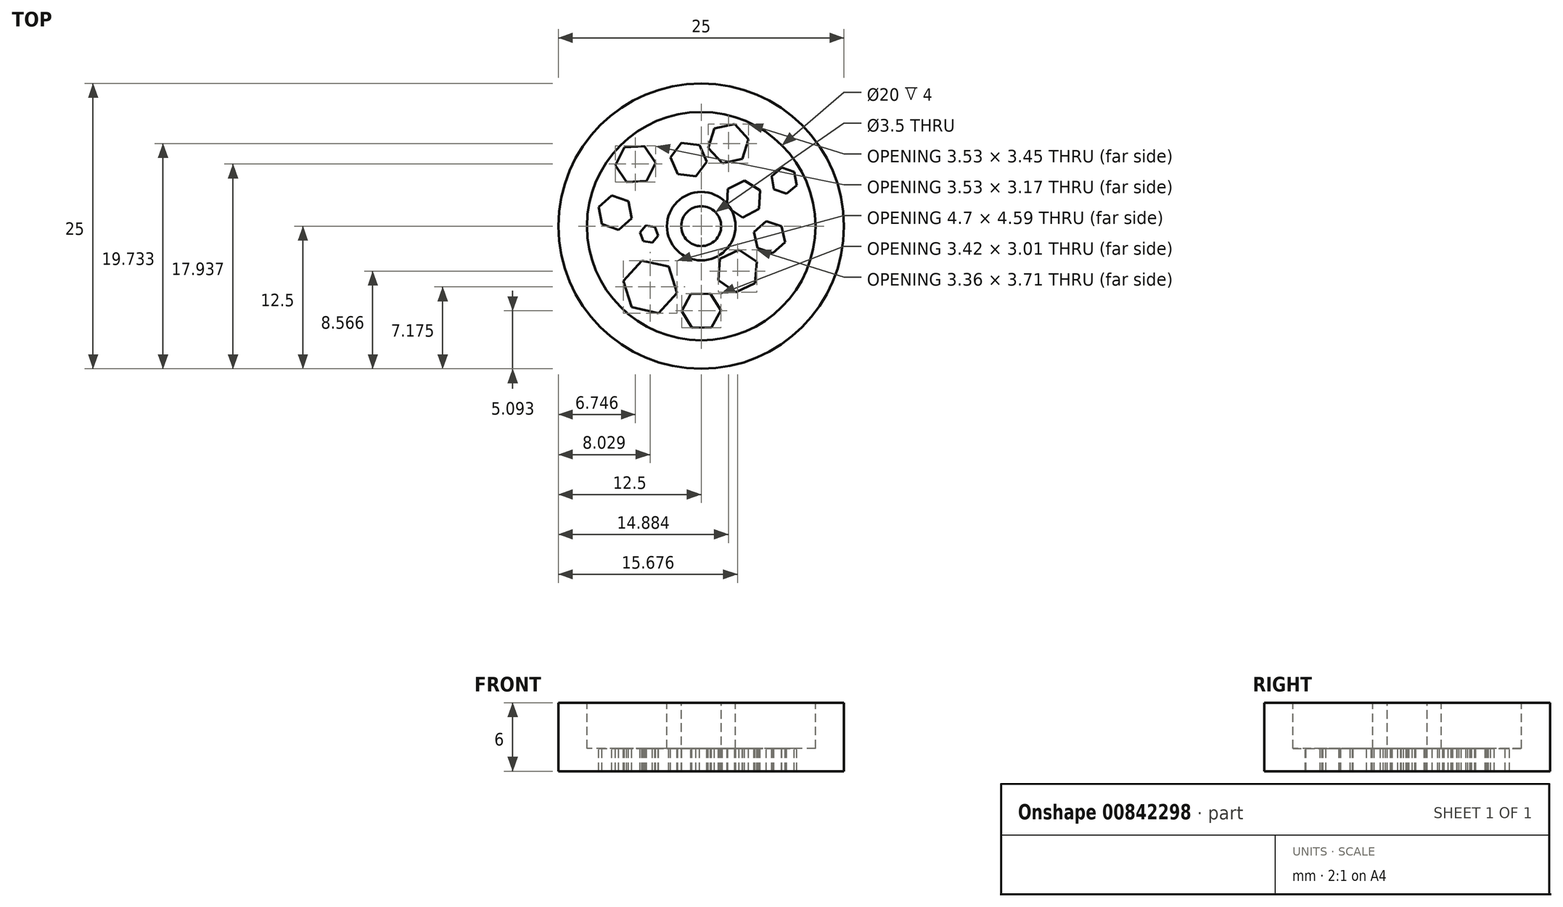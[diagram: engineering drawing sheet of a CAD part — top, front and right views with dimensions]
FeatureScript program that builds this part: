
annotation { "Feature Type Name" : "Feature", "Feature Type Description" : "" }
export const myFeature = defineFeature(function(context is Context, id is Id, definition is map)
    precondition{}
    {
        {
            var Q0;
            Q0=qCreatedBy(makeId("Top.planeOp"),FACE);
            var sketch = newSketch(context, id + "F0", { "sketchPlane" : qUnion([Q0])});
            skCircle(sketch, "E0", {"center": v(0, 0) * mm, "radius": 12.5 * mm});
            skSolve(sketch);
        }
        {
            var Q0;
            Q0 = qSketchRegion(id + "F0", true);
            extrude(context, id + "F1", {"entities" : qUnion([Q0]), "depth" : 6 * mm, "offsetDistance" : 25 * mm});
        }
        {
            var Q0;
            Q0=makeQuery(id+"F1.opExtrude","CAP_FACE",FACE,{"disambiguationData":[OSD([sQuery(id+"F0.wireOp",EDGE,"E0")])],"isStart":false});
            var sketch = newSketch(context, id + "F2", { "sketchPlane" : qUnion([Q0])});
            skCircle(sketch, "E1", {"center": v(0, 0) * mm, "radius": 10 * mm});
            skCircle(sketch, "E2", {"center": v(0, 0) * mm, "radius": 3 * mm});
            skSolve(sketch);
        }
        {
            var Q0;
            Q0 = qSketchRegion(id + "F2", true);
            extrude(context, id + "F3", {"entities" : qUnion([Q0]), "operationType" : NewBodyOperationType.REMOVE, "oppositeDirection" : true, "depth" : 4 * mm, "offsetDistance" : 25 * mm});
        }
        {
            var Q0;
            Q0=makeQuery(id+"F3.boolean.opBoolean","SPLIT",FACE,{"disambiguationData":[TD([makeQuery(id+"F3.opExtrude","SWEPT_FACE",FACE,{"disambiguationData":[OSD([sQuery(id+"F2.wireOp",EDGE,"E2")])]})])],"derivedFrom":makeQuery(id+"F1.opExtrude","CAP_FACE",FACE,{"disambiguationData":[OSD([sQuery(id+"F0.wireOp",EDGE,"E0")])],"isStart":false})});
            var sketch = newSketch(context, id + "F4", { "sketchPlane" : qUnion([Q0])});
            skPoint(sketch, "E3", {"position": v(0, 0) * mm});
            skSolve(sketch);
        }
        {
            var Q0;
            Q0=sQuery(id+"F4.wireOp",VERTEX,"E3");
            var Q1;
            Q1=makeQuery(id+"F1.opExtrude","SWEPT_BODY",BODY,{"disambiguationData":[OSD([sQuery(id+"F0.wireOp",EDGE,"E0")])]});
            hole(context, id + "F5", {"style" : HoleStyle.SIMPLE, "endStyle" : HoleEndStyle.THROUGH, "holeDiameter" : 3.5 * mm, "majorDiameter" : 5 * mm, "isTappedThrough" : true, "tappedDepth" : 12 * mm, "tapClearance" : 3, "locations" : qUnion([Q0]), "scope" : qUnion([Q1])});
        }
        {
            var Q0;
            Q0=makeQuery(id+"F3.boolean.opBoolean","COPY",FACE,{"derivedFrom":makeQuery(id+"F3.opExtrude","CAP_FACE",FACE,{"disambiguationData":[OSD([sQuery(id+"F2.wireOp",EDGE,"E1"),sQuery(id+"F2.wireOp",EDGE,"E2")])],"isStart":false})});
            var sketch = newSketch(context, id + "F6", { "sketchPlane" : qUnion([Q0])});
            skCircle(sketch, "E4.cCircle", {"center": v(-7.53, 1.18) * mm, "radius": 1.53 * mm, "construction": true});
            skLineSegment(sketch, "E4.0", {"start": v(-6.38, 2.2) * mm, "end": v(-6.08, 0.69) * mm});
            skLineSegment(sketch, "E4.1", {"start": v(-6.08, 0.69) * mm, "end": v(-7.23, -0.32) * mm});
            skLineSegment(sketch, "E4.2", {"start": v(-7.23, -0.32) * mm, "end": v(-8.68, 0.17) * mm});
            skLineSegment(sketch, "E4.3", {"start": v(-8.68, 0.17) * mm, "end": v(-8.98, 1.67) * mm});
            skLineSegment(sketch, "E4.4", {"start": v(-8.98, 1.67) * mm, "end": v(-7.83, 2.68) * mm});
            skLineSegment(sketch, "E4.5", {"start": v(-7.83, 2.68) * mm, "end": v(-6.38, 2.2) * mm});
            skCircle(sketch, "E5.cCircle", {"center": v(-4.47, -5.32) * mm, "radius": 2.4 * mm, "construction": true});
            skLineSegment(sketch, "E5.0", {"start": v(-2.12, -5.85) * mm, "end": v(-3.75, -7.62) * mm});
            skLineSegment(sketch, "E5.1", {"start": v(-3.75, -7.62) * mm, "end": v(-6.1, -7.1) * mm});
            skLineSegment(sketch, "E5.2", {"start": v(-6.1, -7.1) * mm, "end": v(-6.82, -4.8) * mm});
            skLineSegment(sketch, "E5.3", {"start": v(-6.82, -4.8) * mm, "end": v(-5.2, -3.03) * mm});
            skLineSegment(sketch, "E5.4", {"start": v(-5.2, -3.03) * mm, "end": v(-2.84, -3.55) * mm});
            skLineSegment(sketch, "E5.5", {"start": v(-2.84, -3.55) * mm, "end": v(-2.12, -5.85) * mm});
            skCircle(sketch, "E6.cCircle", {"center": v(-5.75, 5.44) * mm, "radius": 1.77 * mm, "construction": true});
            skLineSegment(sketch, "E6.0", {"start": v(-4, 5.55) * mm, "end": v(-4.77, 3.97) * mm});
            skLineSegment(sketch, "E6.1", {"start": v(-4.77, 3.97) * mm, "end": v(-6.54, 3.85) * mm});
            skLineSegment(sketch, "E6.2", {"start": v(-6.54, 3.85) * mm, "end": v(-7.52, 5.32) * mm});
            skLineSegment(sketch, "E6.3", {"start": v(-7.52, 5.32) * mm, "end": v(-6.73, 6.9) * mm});
            skLineSegment(sketch, "E6.4", {"start": v(-6.73, 6.9) * mm, "end": v(-4.97, 7.02) * mm});
            skLineSegment(sketch, "E6.5", {"start": v(-4.97, 7.02) * mm, "end": v(-4, 5.55) * mm});
            skCircle(sketch, "E7.cCircle", {"center": v(-1.1, 5.83) * mm, "radius": 1.6 * mm, "construction": true});
            skLineSegment(sketch, "E7.0", {"start": v(0.47, 5.65) * mm, "end": v(-0.48, 4.37) * mm});
            skLineSegment(sketch, "E7.1", {"start": v(-0.48, 4.37) * mm, "end": v(-2.06, 4.55) * mm});
            skLineSegment(sketch, "E7.2", {"start": v(-2.06, 4.55) * mm, "end": v(-2.7, 6.01) * mm});
            skLineSegment(sketch, "E7.3", {"start": v(-2.7, 6.01) * mm, "end": v(-1.74, 7.3) * mm});
            skLineSegment(sketch, "E7.4", {"start": v(-1.74, 7.3) * mm, "end": v(-0.16, 7.1) * mm});
            skLineSegment(sketch, "E7.5", {"start": v(-0.16, 7.1) * mm, "end": v(0.47, 5.65) * mm});
            skCircle(sketch, "E8.cCircle", {"center": v(2.38, 7.23) * mm, "radius": 1.8 * mm, "construction": true});
            skLineSegment(sketch, "E8.0", {"start": v(3.6, 5.9) * mm, "end": v(1.84, 5.5) * mm});
            skLineSegment(sketch, "E8.1", {"start": v(1.84, 5.5) * mm, "end": v(0.62, 6.85) * mm});
            skLineSegment(sketch, "E8.2", {"start": v(0.62, 6.85) * mm, "end": v(1.17, 8.57) * mm});
            skLineSegment(sketch, "E8.3", {"start": v(1.17, 8.57) * mm, "end": v(2.93, 8.96) * mm});
            skLineSegment(sketch, "E8.4", {"start": v(2.93, 8.96) * mm, "end": v(4.15, 7.62) * mm});
            skLineSegment(sketch, "E8.5", {"start": v(4.15, 7.62) * mm, "end": v(3.6, 5.9) * mm});
            skCircle(sketch, "E9.cCircle", {"center": v(3.7, 2.38) * mm, "radius": 1.62 * mm, "construction": true});
            skLineSegment(sketch, "E9.0", {"start": v(5.07, 1.5) * mm, "end": v(3.63, 0.76) * mm});
            skLineSegment(sketch, "E9.1", {"start": v(3.63, 0.76) * mm, "end": v(2.26, 1.63) * mm});
            skLineSegment(sketch, "E9.2", {"start": v(2.26, 1.63) * mm, "end": v(2.34, 3.25) * mm});
            skLineSegment(sketch, "E9.3", {"start": v(2.34, 3.25) * mm, "end": v(3.78, 4) * mm});
            skLineSegment(sketch, "E9.4", {"start": v(3.78, 4) * mm, "end": v(5.14, 3.12) * mm});
            skLineSegment(sketch, "E9.5", {"start": v(5.14, 3.12) * mm, "end": v(5.07, 1.5) * mm});
            skCircle(sketch, "E10.cCircle", {"center": v(3.18, -3.93) * mm, "radius": 1.86 * mm, "construction": true});
            skLineSegment(sketch, "E10.0", {"start": v(4.86, -3.14) * mm, "end": v(4.7, -5) * mm});
            skLineSegment(sketch, "E10.1", {"start": v(4.7, -5) * mm, "end": v(3.03, -5.79) * mm});
            skLineSegment(sketch, "E10.2", {"start": v(3.03, -5.79) * mm, "end": v(1.5, -4.73) * mm});
            skLineSegment(sketch, "E10.3", {"start": v(1.5, -4.73) * mm, "end": v(1.64, -2.88) * mm});
            skLineSegment(sketch, "E10.4", {"start": v(1.64, -2.88) * mm, "end": v(3.33, -2.08) * mm});
            skLineSegment(sketch, "E10.5", {"start": v(3.33, -2.08) * mm, "end": v(4.86, -3.14) * mm});
            skCircle(sketch, "E11.cCircle", {"center": v(5.98, -0.95) * mm, "radius": 1.42 * mm, "construction": true});
            skLineSegment(sketch, "E11.0", {"start": v(7.03, 0) * mm, "end": v(7.33, -1.4) * mm});
            skLineSegment(sketch, "E11.1", {"start": v(7.33, -1.4) * mm, "end": v(6.27, -2.34) * mm});
            skLineSegment(sketch, "E11.2", {"start": v(6.27, -2.34) * mm, "end": v(4.92, -1.9) * mm});
            skLineSegment(sketch, "E11.3", {"start": v(4.92, -1.9) * mm, "end": v(4.62, -0.51) * mm});
            skLineSegment(sketch, "E11.4", {"start": v(4.62, -0.51) * mm, "end": v(5.68, 0.44) * mm});
            skLineSegment(sketch, "E11.5", {"start": v(5.68, 0.44) * mm, "end": v(7.03, 0) * mm});
            skCircle(sketch, "E12.cCircle", {"center": v(-4.56, -0.7) * mm, "radius": 0.8 * mm, "construction": true});
            skLineSegment(sketch, "E12.0", {"start": v(-3.77, -0.84) * mm, "end": v(-4.29, -1.45) * mm});
            skLineSegment(sketch, "E12.1", {"start": v(-4.29, -1.45) * mm, "end": v(-5.08, -1.3) * mm});
            skLineSegment(sketch, "E12.2", {"start": v(-5.08, -1.3) * mm, "end": v(-5.35, -0.55) * mm});
            skLineSegment(sketch, "E12.3", {"start": v(-5.35, -0.55) * mm, "end": v(-4.83, 0.06) * mm});
            skLineSegment(sketch, "E12.4", {"start": v(-4.83, 0.06) * mm, "end": v(-4.05, -0.08) * mm});
            skLineSegment(sketch, "E12.5", {"start": v(-4.05, -0.08) * mm, "end": v(-3.77, -0.84) * mm});
            skCircle(sketch, "E13.cCircle", {"center": v(0, -7.4) * mm, "radius": 1.71 * mm, "construction": true});
            skPoint(sketch, "E13.cCircle.perimeterSnap0", {"position": v(-4.92, -7.36) * mm});
            skLineSegment(sketch, "E13.0", {"start": v(1.71, -7.36) * mm, "end": v(0.9, -8.87) * mm});
            skPoint(sketch, "E13.0.startSnap0", {"position": v(-4.92, -7.36) * mm});
            skLineSegment(sketch, "E13.1", {"start": v(0.9, -8.87) * mm, "end": v(-0.82, -8.91) * mm});
            skLineSegment(sketch, "E13.2", {"start": v(-0.82, -8.91) * mm, "end": v(-1.71, -7.45) * mm});
            skLineSegment(sketch, "E13.3", {"start": v(-1.71, -7.45) * mm, "end": v(-0.9, -5.95) * mm});
            skLineSegment(sketch, "E13.4", {"start": v(-0.9, -5.95) * mm, "end": v(0.82, -5.9) * mm});
            skLineSegment(sketch, "E13.5", {"start": v(0.82, -5.9) * mm, "end": v(1.71, -7.36) * mm});
            skCircle(sketch, "E14.cCircle", {"center": v(7.25, 3.99) * mm, "radius": 1.17 * mm, "construction": true});
            skLineSegment(sketch, "E14.0", {"start": v(7.46, 2.84) * mm, "end": v(6.36, 3.24) * mm});
            skLineSegment(sketch, "E14.1", {"start": v(6.36, 3.24) * mm, "end": v(6.16, 4.39) * mm});
            skLineSegment(sketch, "E14.2", {"start": v(6.16, 4.39) * mm, "end": v(7.05, 5.14) * mm});
            skLineSegment(sketch, "E14.3", {"start": v(7.05, 5.14) * mm, "end": v(8.15, 4.74) * mm});
            skLineSegment(sketch, "E14.4", {"start": v(8.15, 4.74) * mm, "end": v(8.35, 3.6) * mm});
            skLineSegment(sketch, "E14.5", {"start": v(8.35, 3.6) * mm, "end": v(7.46, 2.84) * mm});
            skSolve(sketch);
        }
        {
            var Q0;
            Q0 = qSketchRegion(id + "F6", true);
            extrude(context, id + "F7", {"entities" : qUnion([Q0]), "operationType" : NewBodyOperationType.REMOVE, "oppositeDirection" : true, "depth" : 25 * mm, "offsetDistance" : 25 * mm});
        }
        {
            var Q0;
            Q0 = qSketchRegion(id + "F6", true);
            extrude(context, id + "F8", {"entities" : qUnion([Q0]), "operationType" : NewBodyOperationType.REMOVE, "oppositeDirection" : true, "depth" : 25 * mm, "offsetDistance" : 25 * mm});
        }
        {
            var Q0;
            Q0 = qSketchRegion(id + "F6", true);
            extrude(context, id + "F9", {"entities" : qUnion([Q0]), "operationType" : NewBodyOperationType.REMOVE, "oppositeDirection" : true, "depth" : 25 * mm, "offsetDistance" : 25 * mm});
        }
    });
